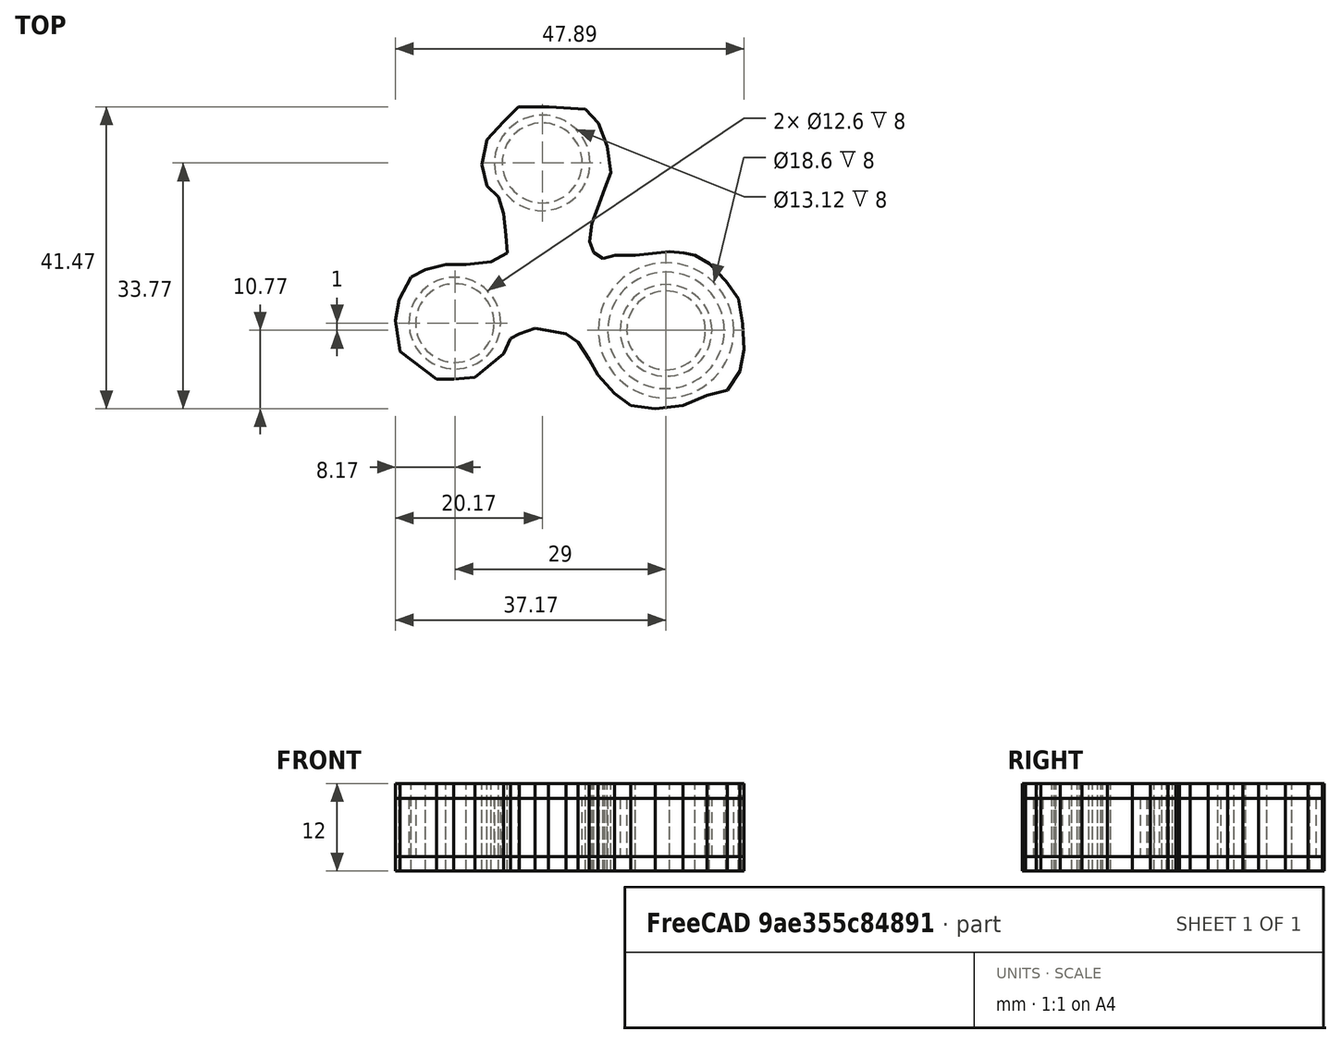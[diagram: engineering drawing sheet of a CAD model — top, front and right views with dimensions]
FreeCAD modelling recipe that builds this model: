
FCSTD DOCUMENT  (FreeCAD 0.20R29603 (Git))
Label: fitment-test
License: All rights reserved
LicenseURL: http://en.wikipedia.org/wiki/All_rights_reserved
objects: Part::Cylinder×8, Part::Cut×5, Sketcher::SketchObject×1, PartDesign::Pad×1, PartDesign::Body×1, App::Part×1, Part::MultiFuse×1
note: 18 computed .brp shape members not serialized (recipe doc carries the construction recipe); baked Part::Feature solids carry a one-line shape summary decoded from their .brp

FEATURE [Part::Cylinder] Cylinder  label="outside"
  Angle = 360
  AttacherType = Attacher::AttachEngine3D
  FirstAngle = 0
  Height = 8
  Radius = 9.3
  SecondAngle = 0
FEATURE [Part::Cylinder] Cylinder001  label="inside"
  Angle = 360
  AttacherType = Attacher::AttachEngine3D
  FirstAngle = 0
  Height = 8
  Radius = 8
  SecondAngle = 0
FEATURE [Part::Cut] Cut  label="socket-cutout-big"
  Base = -> Cylinder
  Placement = pos=(24,-4,0) rot=(0,0,1;0rad)
  Tool = -> Cylinder001
FEATURE [Part::Cylinder] Cylinder002  label="medium-outside"
  Angle = 360
  AttacherType = Attacher::AttachEngine3D
  FirstAngle = 0
  Height = 8
  Radius = 6.56
  SecondAngle = 0
FEATURE [Part::Cylinder] Cylinder003  label="medium-inside"
  Angle = 360
  AttacherType = Attacher::AttachEngine3D
  FirstAngle = 0
  Height = 8
  Radius = 5.5
  SecondAngle = 0
FEATURE [Part::Cut] Cut001  label="socket-cutout-medium"
  Base = -> Cylinder002
  Placement = pos=(7,19,0) rot=(0,0,1;0rad)
  Tool = -> Cylinder003
FEATURE [Part::Cylinder] Cylinder004  label="outside-small"
  Angle = 360
  AttacherType = Attacher::AttachEngine3D
  FirstAngle = 0
  Height = 8
  Radius = 6.3
  SecondAngle = 0
FEATURE [Part::Cylinder] Cylinder005  label="inside-small"
  Angle = 360
  AttacherType = Attacher::AttachEngine3D
  FirstAngle = 0
  Height = 8
  Radius = 5.4
  SecondAngle = 0
FEATURE [Part::Cut] Cut002  label="socket-cutout-small"
  Base = -> Cylinder004
  Placement = pos=(-5,-3,0) rot=(0,0,1;0rad)
  Tool = -> Cylinder005
FEATURE [Sketcher::SketchObject] Sketch
  FullyConstrained = false
  MapMode = 5
  Support = -> [XY_Plane002]
  sketch-geometry (57):
    g0: LineSegment StartX=12.9019 StartY=26.4026 StartZ=0 EndX=14.6951 EndY=24.4599 EndZ=0
    g1: LineSegment StartX=14.6951 StartY=24.4599 StartZ=0 EndX=15.8906 EndY=21.3217 EndZ=0
    g2: LineSegment StartX=15.8906 StartY=21.3217 StartZ=0 EndX=16.4137 EndY=17.6606 EndZ=0
    g3: LineSegment StartX=16.4137 StartY=17.6606 StartZ=0 EndX=15.5918 EndY=15.4937 EndZ=0
    g4: LineSegment StartX=15.5918 StartY=15.4937 StartZ=0 EndX=14.8446 EndY=13.4016 EndZ=0
    g5: LineSegment StartX=14.8446 StartY=13.4016 StartZ=0 EndX=13.7985 EndY=10.7118 EndZ=0
    g6: LineSegment StartX=13.7985 StartY=10.7118 StartZ=0 EndX=13.4997 EndY=8.24607 EndZ=0
    g7: LineSegment StartX=13.4997 StartY=8.24607 StartZ=0 EndX=14.0974 EndY=6.67699 EndZ=0
    g8: LineSegment StartX=14.0974 StartY=6.67699 StartZ=0 EndX=15.3676 EndY=5.85509 EndZ=0
    g9: LineSegment StartX=15.3676 StartY=5.85509 StartZ=0 EndX=17.0114 EndY=6.3034 EndZ=0
    g10: LineSegment StartX=17.0114 StartY=6.3034 StartZ=0 EndX=19.776 EndY=6.3034 EndZ=0
    g11: LineSegment StartX=19.776 StartY=6.3034 StartZ=0 EndX=24.4832 EndY=6.82643 EndZ=0
    g12: LineSegment StartX=24.4832 StartY=6.82643 StartZ=0 EndX=26.4259 EndY=6.60227 EndZ=0
    g13: LineSegment StartX=26.4259 StartY=6.60227 StartZ=0 EndX=27.995 EndY=6.3034 EndZ=0
    g14: LineSegment StartX=27.995 StartY=6.3034 StartZ=0 EndX=29.9376 EndY=5.18263 EndZ=0
    g15: LineSegment StartX=29.9376 StartY=5.18263 StartZ=0 EndX=32.2539 EndY=2.79165 EndZ=0
    g16: LineSegment StartX=32.2539 StartY=2.79165 StartZ=0 EndX=33.9724 EndY=0.325949 EndZ=0
    g17: LineSegment StartX=33.9724 StartY=0.325949 StartZ=0 EndX=34.4955 EndY=-3.11109 EndZ=0
    g18: LineSegment StartX=34.4955 StartY=-3.11109 StartZ=0 EndX=34.7196 EndY=-6.62284 EndZ=0
    g19: LineSegment StartX=34.7196 StartY=-6.62284 StartZ=0 EndX=34.1219 EndY=-9.61157 EndZ=0
    g20: LineSegment StartX=34.1219 StartY=-9.61157 StartZ=0 EndX=32.4033 EndY=-12.2267 EndZ=0
    g21: LineSegment StartX=32.4033 StartY=-12.2267 StartZ=0 EndX=29.6388 EndY=-12.8992 EndZ=0
    g22: LineSegment StartX=29.6388 StartY=-12.8992 StartZ=0 EndX=26.3512 EndY=-14.3188 EndZ=0
    g23: LineSegment StartX=26.3512 StartY=-14.3188 StartZ=0 EndX=22.5405 EndY=-14.7671 EndZ=0
    g24: LineSegment StartX=22.5405 StartY=-14.7671 StartZ=0 EndX=19.1782 EndY=-14.3188 EndZ=0
    g25: LineSegment StartX=19.1782 StartY=-14.3188 StartZ=0 EndX=16.9367 EndY=-12.675 EndZ=0
    g26: LineSegment StartX=16.9367 StartY=-12.675 StartZ=0 EndX=14.6204 EndY=-10.1346 EndZ=0
    g27: LineSegment StartX=14.6204 StartY=-10.1346 StartZ=0 EndX=13.4249 EndY=-7.96776 EndZ=0
    g28: LineSegment StartX=13.4249 StartY=-7.96776 StartZ=0 EndX=11.9306 EndY=-5.6515 EndZ=0
    g29: LineSegment StartX=11.9306 StartY=-5.6515 StartZ=0 EndX=10.2868 EndY=-4.45601 EndZ=0
    g30: LineSegment StartX=10.2868 StartY=-4.45601 StartZ=0 EndX=7.82107 EndY=-4.0077 EndZ=0
    g31: LineSegment StartX=7.82107 StartY=-4.0077 StartZ=0 EndX=6.02784 EndY=-3.70883 EndZ=0
    g32: LineSegment StartX=6.02784 StartY=-3.70883 StartZ=0 EndX=3.86101 EndY=-4.45601 EndZ=0
    g33: LineSegment StartX=3.86101 StartY=-4.45601 StartZ=0 EndX=2.66552 EndY=-5.12848 EndZ=0
    g34: LineSegment StartX=2.66552 StartY=-5.12848 StartZ=0 EndX=1.69419 EndY=-7.22058 EndZ=0
    g35: LineSegment StartX=1.69419 StartY=-7.22058 StartZ=0 EndX=-2.26588 EndY=-10.4335 EndZ=0
    g36: LineSegment StartX=-2.26588 StartY=-10.4335 StartZ=0 EndX=-5.17988 EndY=-10.7323 EndZ=0
    g37: LineSegment StartX=-5.17988 StartY=-10.7323 StartZ=0 EndX=-7.49615 EndY=-10.7323 EndZ=0
    g38: LineSegment StartX=-7.49615 StartY=-10.7323 StartZ=0 EndX=-12.5023 EndY=-6.92171 EndZ=0
    g39: LineSegment StartX=-12.5023 StartY=-6.92171 StartZ=0 EndX=-13.1747 EndY=-2.66278 EndZ=0
    g40: LineSegment StartX=-13.1747 StartY=-2.66278 StartZ=0 EndX=-12.6517 EndY=0.251231 EndZ=0
    g41: LineSegment StartX=-12.6517 StartY=0.251231 StartZ=0 EndX=-11.0079 EndY=3.31467 EndZ=0
    g42: LineSegment StartX=-11.0079 StartY=3.31467 StartZ=0 EndX=-9.06523 EndY=4.36073 EndZ=0
    g43: LineSegment StartX=-9.06523 StartY=4.36073 StartZ=0 EndX=-6.22594 EndY=5.03319 EndZ=0
    g44: LineSegment StartX=-6.22594 StartY=5.03319 StartZ=0 EndX=-3.46137 EndY=5.03319 EndZ=0
    g45: LineSegment StartX=-3.46137 StartY=5.03319 StartZ=0 EndX=0 EndY=5.40678 EndZ=0
    g46: LineSegment StartX=0 StartY=5.40678 StartZ=0 EndX=2.21721 EndY=6.60227 EndZ=0
    g47: LineSegment StartX=2.21721 StartY=6.60227 StartZ=0 EndX=1.99306 EndY=9.06797 EndZ=0
    g48: LineSegment StartX=1.99306 StartY=9.06797 StartZ=0 EndX=1.69419 EndY=12.0567 EndZ=0
    g49: LineSegment StartX=1.69419 StartY=12.0567 StartZ=0 EndX=1.02172 EndY=14.2982 EndZ=0
    g50: LineSegment StartX=1.02172 StartY=14.2982 StartZ=0 EndX=-0.622075 EndY=15.8673 EndZ=0
    g51: LineSegment StartX=-0.622075 StartY=15.8673 StartZ=0 EndX=-1.29454 EndY=18.7813 EndZ=0
    g52: LineSegment StartX=1.69419 StartY=24.6841 StartZ=0 EndX=3.71157 EndY=26.7015 EndZ=0
    g53: LineSegment StartX=3.71157 StartY=26.7015 StartZ=0 EndX=7.89579 EndY=26.7015 EndZ=0
    g54: LineSegment StartX=7.89579 StartY=26.7015 StartZ=0 EndX=12.9019 EndY=26.4026 EndZ=0
    g55: LineSegment StartX=1.69419 StartY=24.6841 StartZ=0 EndX=-0.622075 EndY=22.2184 EndZ=0
    g56: LineSegment StartX=-0.622075 StartY=22.2184 StartZ=0 EndX=-1.29454 EndY=18.7813 EndZ=0
  constraints (62):
    c: Coincident(g0,g1)
    c: Coincident(g1,g2)
    c: Coincident(g2,g3)
    c: Coincident(g3,g4)
    c: Coincident(g4,g5)
    c: Coincident(g5,g6)
    c: Coincident(g6,g7)
    c: Coincident(g7,g8)
    c: Coincident(g8,g9)
    c: Coincident(g9,g10)
    c: Horizontal(g10)
    c: Coincident(g10,g11)
    c: Coincident(g11,g12)
    c: Coincident(g12,g13)
    c: Coincident(g13,g14)
    c: Coincident(g14,g15)
    c: Coincident(g15,g16)
    c: Coincident(g16,g17)
    c: Coincident(g17,g18)
    c: Coincident(g18,g19)
    c: Coincident(g19,g20)
    c: Coincident(g20,g21)
    c: Coincident(g21,g22)
    c: Coincident(g22,g23)
    c: Coincident(g23,g24)
    c: Coincident(g24,g25)
    c: Coincident(g25,g26)
    c: Coincident(g26,g27)
    c: Coincident(g27,g28)
    c: Coincident(g28,g29)
    c: Coincident(g29,g30)
    c: Coincident(g30,g31)
    c: Coincident(g31,g32)
    c: Coincident(g32,g33)
    c: Coincident(g33,g34)
    c: Coincident(g34,g35)
    c: Coincident(g35,g36)
    c: Coincident(g36,g37)
    c: Horizontal(g37)
    c: Coincident(g37,g38)
    c: Coincident(g38,g39)
    c: Coincident(g39,g40)
    c: Coincident(g40,g41)
    c: Coincident(g41,g42)
    c: Coincident(g42,g43)
    c: Coincident(g43,g44)
    c: Horizontal(g44)
    c: Coincident(g44,g45)
    c: PointOnObject(g45,g-2)
    c: Coincident(g45,g46)
    c: Coincident(g46,g47)
    c: Coincident(g47,g48)
    c: Coincident(g48,g49)
    c: Coincident(g49,g50)
    c: Coincident(g50,g51)
    c: Coincident(g52,g53)
    c: Horizontal(g53)
    c: Coincident(g53,g54)
    c: Coincident(g54,g0)
    c: Coincident(g52,g55)
    c: Coincident(g55,g56)
    c: Coincident(g56,g51)
FEATURE [PartDesign::Pad] Pad
  Direction = (0,0,1)
  Length = 10
  Length2 = 10
  Profile = -> Sketch
  ReferenceAxis = -> Sketch [N_Axis]
  Type = 0
FEATURE [PartDesign::Body] Body
  Group = -> [Sketch,Pad]
  Origin = -> Origin002
  Tip = -> Pad
FEATURE [App::Part] Part001  label="surround"
  Group = -> [Body]
  Origin = -> Origin001
  Placement = pos=(0,0,-2) rot=(0,0,1;0rad)
FEATURE [Part::Cylinder] Cylinder006  label="outside-small001"
  Angle = 360
  AttacherType = Attacher::AttachEngine3D
  FirstAngle = 0
  Height = 8
  Radius = 6.3
  SecondAngle = 0
FEATURE [Part::Cylinder] Cylinder007  label="inside-small001"
  Angle = 360
  AttacherType = Attacher::AttachEngine3D
  FirstAngle = 0
  Height = 8
  Radius = 5.4
  SecondAngle = 0
FEATURE [Part::Cut] Cut003  label="socket-cutout-small001"
  Base = -> Cylinder006
  Placement = pos=(24,-4,0) rot=(0,0,1;0rad)
  Tool = -> Cylinder007
FEATURE [Part::MultiFuse] Fusion
  Shapes = -> [Cut003,Cut,Cut002,Cut001]
FEATURE [Part::Cut] Cut004  label="fitment-test"
  Base = -> Part001
  Tool = -> Fusion
